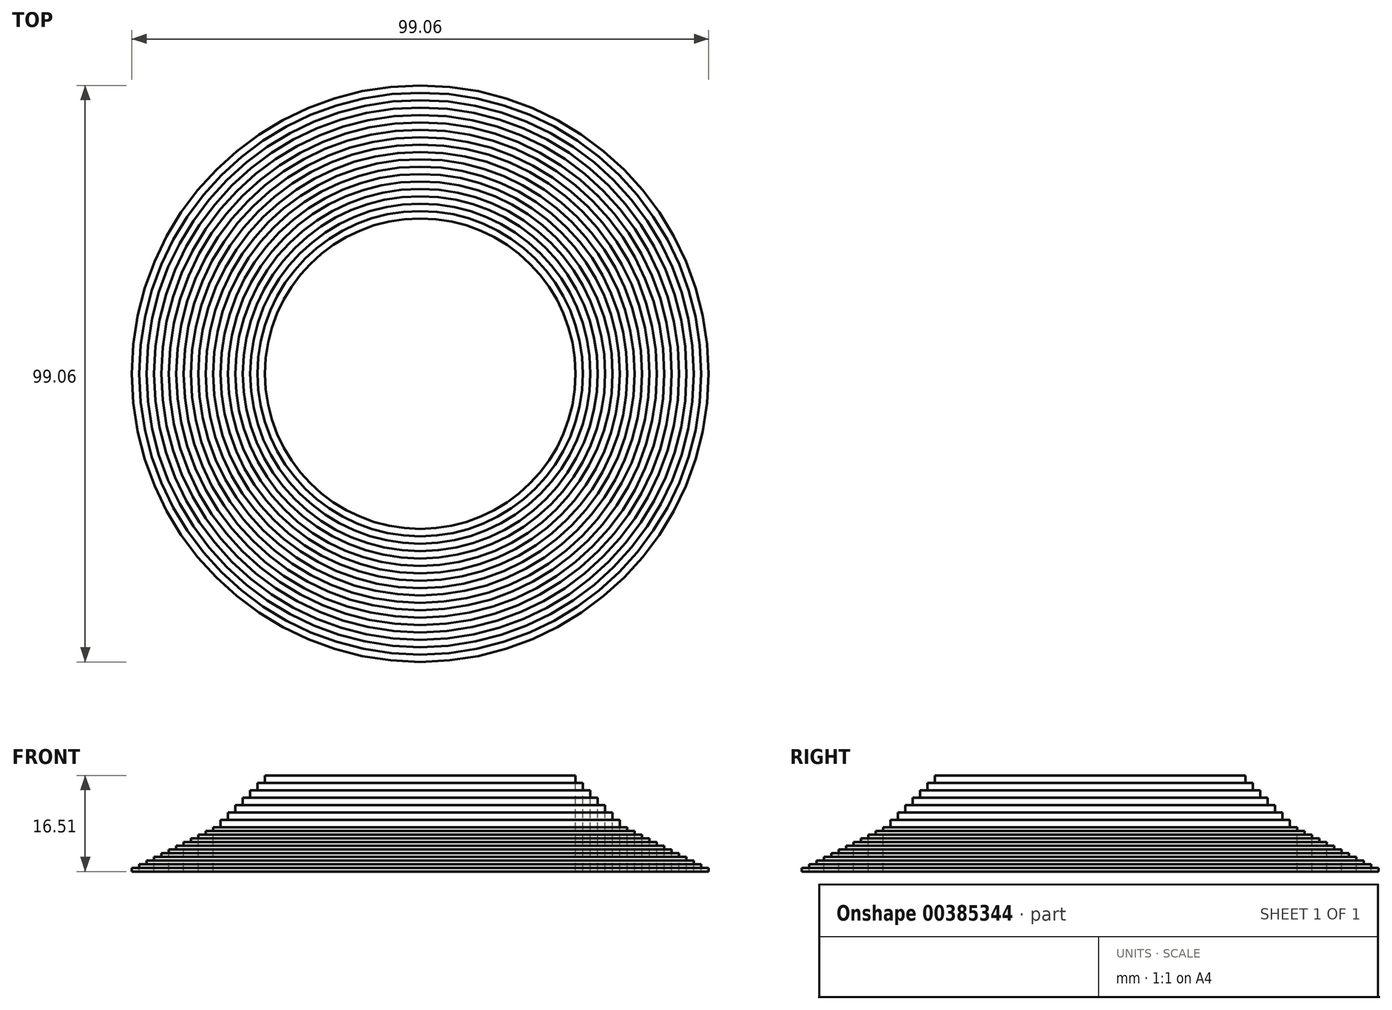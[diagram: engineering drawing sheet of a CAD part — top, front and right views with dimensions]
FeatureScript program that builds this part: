
annotation { "Feature Type Name" : "Feature", "Feature Type Description" : "" }
export const myFeature = defineFeature(function(context is Context, id is Id, definition is map)
    precondition{}
    {
        {
            var Q0;
            Q0=qCreatedBy(makeId("Top.planeOp"),FACE);
            var sketch = newSketch(context, id + "F0", { "sketchPlane" : qUnion([Q0])});
            skCircle(sketch, "E0", {"center": v(0, 0) * mm, "radius": 50.8 * mm});
            skSolve(sketch);
        }
        {
            var Q0;
            Q0=makeQuery(id+"F0.imprint","IMPRINT",FACE,{"disambiguationData":[TD([[makeQuery(id+"F0.imprint","IMPRINT",EDGE,{"derivedFrom":sQuery(id+"F0.wireOp",EDGE,"E0")}),1.0]])]});
            var sketch = newSketch(context, id + "F1", { "sketchPlane" : qUnion([Q0])});
            skCircle(sketch, "E1", {"center": v(0, 0) * mm, "radius": 49.53 * mm});
            skSolve(sketch);
        }
        {
            var Q0;
            Q0=sQuery(id+"F1.wireOp",EDGE,"E1");
            extrude(context, id + "F2", {"bodyType" : ToolBodyType.SURFACE, "surfaceEntities" : qUnion([Q0]), "depth" : 0.64 * mm});
        }
        {
            var Q0;
            Q0=makeQuery(id+"F0.imprint","IMPRINT",FACE,{"disambiguationData":[TD([[makeQuery(id+"F0.imprint","IMPRINT",EDGE,{"derivedFrom":sQuery(id+"F0.wireOp",EDGE,"E0")}),1.0]])]});
            var sketch = newSketch(context, id + "F3", { "sketchPlane" : qUnion([Q0])});
            skCircle(sketch, "E2", {"center": v(0, 0) * mm, "radius": 48.26 * mm});
            skSolve(sketch);
        }
        {
            var Q0;
            Q0=sQuery(id+"F3.wireOp",EDGE,"E2");
            extrude(context, id + "F4", {"bodyType" : ToolBodyType.SURFACE, "surfaceEntities" : qUnion([Q0]), "depth" : 1.27 * mm});
        }
        {
            var Q0;
            Q0=makeQuery(id+"F0.imprint","IMPRINT",FACE,{"disambiguationData":[TD([[makeQuery(id+"F0.imprint","IMPRINT",EDGE,{"derivedFrom":sQuery(id+"F0.wireOp",EDGE,"E0")}),1.0]])]});
            var sketch = newSketch(context, id + "F5", { "sketchPlane" : qUnion([Q0])});
            skCircle(sketch, "E3", {"center": v(0, 0) * mm, "radius": 47 * mm});
            skSolve(sketch);
        }
        {
            var Q0;
            Q0=sQuery(id+"F5.wireOp",EDGE,"E3");
            extrude(context, id + "F6", {"bodyType" : ToolBodyType.SURFACE, "surfaceEntities" : qUnion([Q0]), "depth" : 1.9 * mm});
        }
        {
            var Q0;
            Q0=makeQuery(id+"F0.imprint","IMPRINT",FACE,{"disambiguationData":[TD([[makeQuery(id+"F0.imprint","IMPRINT",EDGE,{"derivedFrom":sQuery(id+"F0.wireOp",EDGE,"E0")}),1.0]])]});
            var sketch = newSketch(context, id + "F7", { "sketchPlane" : qUnion([Q0])});
            skCircle(sketch, "E4", {"center": v(0, 0) * mm, "radius": 45.72 * mm});
            skSolve(sketch);
        }
        {
            var Q0;
            Q0=sQuery(id+"F7.wireOp",EDGE,"E4");
            extrude(context, id + "F8", {"bodyType" : ToolBodyType.SURFACE, "surfaceEntities" : qUnion([Q0]), "depth" : 2.54 * mm});
        }
        {
            var Q0;
            Q0=makeQuery(id+"F0.imprint","IMPRINT",FACE,{"disambiguationData":[TD([[makeQuery(id+"F0.imprint","IMPRINT",EDGE,{"derivedFrom":sQuery(id+"F0.wireOp",EDGE,"E0")}),1.0]])]});
            var sketch = newSketch(context, id + "F9", { "sketchPlane" : qUnion([Q0])});
            skCircle(sketch, "E5", {"center": v(0, 0) * mm, "radius": 44.45 * mm});
            skSolve(sketch);
        }
        {
            var Q0;
            Q0=sQuery(id+"F9.wireOp",EDGE,"E5");
            extrude(context, id + "F10", {"bodyType" : ToolBodyType.SURFACE, "surfaceEntities" : qUnion([Q0]), "depth" : 3.17 * mm});
        }
        {
            var Q0;
            Q0=makeQuery(id+"F0.imprint","IMPRINT",FACE,{"disambiguationData":[TD([[makeQuery(id+"F0.imprint","IMPRINT",EDGE,{"derivedFrom":sQuery(id+"F0.wireOp",EDGE,"E0")}),1.0]])]});
            var sketch = newSketch(context, id + "F11", { "sketchPlane" : qUnion([Q0])});
            skCircle(sketch, "E6", {"center": v(0, 0) * mm, "radius": 43.18 * mm});
            skSolve(sketch);
        }
        {
            var Q0;
            Q0=sQuery(id+"F11.wireOp",EDGE,"E6");
            extrude(context, id + "F12", {"bodyType" : ToolBodyType.SURFACE, "surfaceEntities" : qUnion([Q0]), "depth" : 3.8 * mm});
        }
        {
            var Q0;
            Q0=makeQuery(id+"F0.imprint","IMPRINT",FACE,{"disambiguationData":[TD([[makeQuery(id+"F0.imprint","IMPRINT",EDGE,{"derivedFrom":sQuery(id+"F0.wireOp",EDGE,"E0")}),1.0]])]});
            var sketch = newSketch(context, id + "F13", { "sketchPlane" : qUnion([Q0])});
            skCircle(sketch, "E7", {"center": v(0, 0) * mm, "radius": 41.91 * mm});
            skSolve(sketch);
        }
        {
            var Q0;
            Q0=sQuery(id+"F13.wireOp",EDGE,"E7");
            extrude(context, id + "F14", {"bodyType" : ToolBodyType.SURFACE, "surfaceEntities" : qUnion([Q0]), "depth" : 4.44 * mm});
        }
        {
            var Q0;
            Q0=makeQuery(id+"F0.imprint","IMPRINT",FACE,{"disambiguationData":[TD([[makeQuery(id+"F0.imprint","IMPRINT",EDGE,{"derivedFrom":sQuery(id+"F0.wireOp",EDGE,"E0")}),1.0]])]});
            var sketch = newSketch(context, id + "F15", { "sketchPlane" : qUnion([Q0])});
            skCircle(sketch, "E8", {"center": v(0, 0) * mm, "radius": 40.64 * mm});
            skSolve(sketch);
        }
        {
            var Q0;
            Q0=sQuery(id+"F15.wireOp",EDGE,"E8");
            extrude(context, id + "F16", {"bodyType" : ToolBodyType.SURFACE, "surfaceEntities" : qUnion([Q0]), "depth" : 5.08 * mm});
        }
        {
            var Q0;
            Q0=makeQuery(id+"F0.imprint","IMPRINT",FACE,{"disambiguationData":[TD([[makeQuery(id+"F0.imprint","IMPRINT",EDGE,{"derivedFrom":sQuery(id+"F0.wireOp",EDGE,"E0")}),1.0]])]});
            var sketch = newSketch(context, id + "F17", { "sketchPlane" : qUnion([Q0])});
            skCircle(sketch, "E9", {"center": v(0, 0) * mm, "radius": 39.37 * mm});
            skSolve(sketch);
        }
        {
            var Q0;
            Q0=sQuery(id+"F17.wireOp",EDGE,"E9");
            extrude(context, id + "F18", {"bodyType" : ToolBodyType.SURFACE, "surfaceEntities" : qUnion([Q0]), "depth" : 5.7 * mm});
        }
        {
            var Q0;
            Q0=makeQuery(id+"F0.imprint","IMPRINT",FACE,{"disambiguationData":[TD([[makeQuery(id+"F0.imprint","IMPRINT",EDGE,{"derivedFrom":sQuery(id+"F0.wireOp",EDGE,"E0")}),1.0]])]});
            var sketch = newSketch(context, id + "F19", { "sketchPlane" : qUnion([Q0])});
            skCircle(sketch, "E10", {"center": v(0, 0) * mm, "radius": 38.1 * mm});
            skSolve(sketch);
        }
        {
            var Q0;
            Q0=sQuery(id+"F19.wireOp",EDGE,"E10");
            extrude(context, id + "F20", {"bodyType" : ToolBodyType.SURFACE, "surfaceEntities" : qUnion([Q0]), "depth" : 6.35 * mm});
        }
        {
            var Q0;
            Q0=makeQuery(id+"F0.imprint","IMPRINT",FACE,{"disambiguationData":[TD([[makeQuery(id+"F0.imprint","IMPRINT",EDGE,{"derivedFrom":sQuery(id+"F0.wireOp",EDGE,"E0")}),1.0]])]});
            var sketch = newSketch(context, id + "F21", { "sketchPlane" : qUnion([Q0])});
            skCircle(sketch, "E11", {"center": v(0, 0) * mm, "radius": 36.83 * mm});
            skSolve(sketch);
        }
        {
            var Q0;
            Q0=sQuery(id+"F21.wireOp",EDGE,"E11");
            extrude(context, id + "F22", {"bodyType" : ToolBodyType.SURFACE, "surfaceEntities" : qUnion([Q0]), "depth" : 7 * mm});
        }
        {
            var Q0;
            Q0=makeQuery(id+"F0.imprint","IMPRINT",FACE,{"disambiguationData":[TD([[makeQuery(id+"F0.imprint","IMPRINT",EDGE,{"derivedFrom":sQuery(id+"F0.wireOp",EDGE,"E0")}),1.0]])]});
            var sketch = newSketch(context, id + "F23", { "sketchPlane" : qUnion([Q0])});
            skCircle(sketch, "E12", {"center": v(0, 0) * mm, "radius": 35.56 * mm});
            skSolve(sketch);
        }
        {
            var Q0;
            Q0=sQuery(id+"F23.wireOp",EDGE,"E12");
            extrude(context, id + "F24", {"bodyType" : ToolBodyType.SURFACE, "surfaceEntities" : qUnion([Q0]), "depth" : 7.62 * mm});
        }
        {
            var Q0;
            Q0=makeQuery(id+"F0.imprint","IMPRINT",FACE,{"disambiguationData":[TD([[makeQuery(id+"F0.imprint","IMPRINT",EDGE,{"derivedFrom":sQuery(id+"F0.wireOp",EDGE,"E0")}),1.0]])]});
            var sketch = newSketch(context, id + "F25", { "sketchPlane" : qUnion([Q0])});
            skCircle(sketch, "E13", {"center": v(0, 0) * mm, "radius": 34.3 * mm});
            skSolve(sketch);
        }
        {
            var Q0;
            Q0=sQuery(id+"F25.wireOp",EDGE,"E13");
            extrude(context, id + "F26", {"bodyType" : ToolBodyType.SURFACE, "surfaceEntities" : qUnion([Q0]), "depth" : 8.9 * mm});
        }
        {
            var Q0;
            Q0=makeQuery(id+"F0.imprint","IMPRINT",FACE,{"disambiguationData":[TD([[makeQuery(id+"F0.imprint","IMPRINT",EDGE,{"derivedFrom":sQuery(id+"F0.wireOp",EDGE,"E0")}),1.0]])]});
            var sketch = newSketch(context, id + "F27", { "sketchPlane" : qUnion([Q0])});
            skCircle(sketch, "E14", {"center": v(0, 0) * mm, "radius": 33.02 * mm});
            skSolve(sketch);
        }
        {
            var Q0;
            Q0=sQuery(id+"F27.wireOp",EDGE,"E14");
            extrude(context, id + "F28", {"bodyType" : ToolBodyType.SURFACE, "surfaceEntities" : qUnion([Q0]), "depth" : 10.16 * mm});
        }
        {
            var Q0;
            Q0=makeQuery(id+"F0.imprint","IMPRINT",FACE,{"disambiguationData":[TD([[makeQuery(id+"F0.imprint","IMPRINT",EDGE,{"derivedFrom":sQuery(id+"F0.wireOp",EDGE,"E0")}),1.0]])]});
            var sketch = newSketch(context, id + "F29", { "sketchPlane" : qUnion([Q0])});
            skCircle(sketch, "E15", {"center": v(0, 0) * mm, "radius": 31.75 * mm});
            skSolve(sketch);
        }
        {
            var Q0;
            Q0=sQuery(id+"F29.wireOp",EDGE,"E15");
            extrude(context, id + "F30", {"bodyType" : ToolBodyType.SURFACE, "surfaceEntities" : qUnion([Q0]), "depth" : 11.43 * mm});
        }
        {
            var Q0;
            Q0=makeQuery(id+"F0.imprint","IMPRINT",FACE,{"disambiguationData":[TD([[makeQuery(id+"F0.imprint","IMPRINT",EDGE,{"derivedFrom":sQuery(id+"F0.wireOp",EDGE,"E0")}),1.0]])]});
            var sketch = newSketch(context, id + "F31", { "sketchPlane" : qUnion([Q0])});
            skCircle(sketch, "E16", {"center": v(0, 0) * mm, "radius": 30.48 * mm});
            skSolve(sketch);
        }
        {
            var Q0;
            Q0=sQuery(id+"F31.wireOp",EDGE,"E16");
            extrude(context, id + "F32", {"bodyType" : ToolBodyType.SURFACE, "surfaceEntities" : qUnion([Q0]), "depth" : 12.7 * mm});
        }
        {
            var Q0;
            Q0=makeQuery(id+"F0.imprint","IMPRINT",FACE,{"disambiguationData":[TD([[makeQuery(id+"F0.imprint","IMPRINT",EDGE,{"derivedFrom":sQuery(id+"F0.wireOp",EDGE,"E0")}),1.0]])]});
            var sketch = newSketch(context, id + "F33", { "sketchPlane" : qUnion([Q0])});
            skCircle(sketch, "E17", {"center": v(0, 0) * mm, "radius": 29.21 * mm});
            skSolve(sketch);
        }
        {
            var Q0;
            Q0=sQuery(id+"F33.wireOp",EDGE,"E17");
            extrude(context, id + "F34", {"bodyType" : ToolBodyType.SURFACE, "surfaceEntities" : qUnion([Q0]), "depth" : 13.97 * mm});
        }
        {
            var Q0;
            Q0=makeQuery(id+"F0.imprint","IMPRINT",FACE,{"disambiguationData":[TD([[makeQuery(id+"F0.imprint","IMPRINT",EDGE,{"derivedFrom":sQuery(id+"F0.wireOp",EDGE,"E0")}),1.0]])]});
            var sketch = newSketch(context, id + "F35", { "sketchPlane" : qUnion([Q0])});
            skCircle(sketch, "E18", {"center": v(0, 0) * mm, "radius": 27.94 * mm});
            skSolve(sketch);
        }
        {
            var Q0;
            Q0=sQuery(id+"F35.wireOp",EDGE,"E18");
            extrude(context, id + "F36", {"bodyType" : ToolBodyType.SURFACE, "surfaceEntities" : qUnion([Q0]), "depth" : 15.24 * mm});
        }
        {
            var Q0;
            Q0=makeQuery(id+"F0.imprint","IMPRINT",FACE,{"disambiguationData":[TD([[makeQuery(id+"F0.imprint","IMPRINT",EDGE,{"derivedFrom":sQuery(id+"F0.wireOp",EDGE,"E0")}),1.0]])]});
            var sketch = newSketch(context, id + "F37", { "sketchPlane" : qUnion([Q0])});
            skCircle(sketch, "E19", {"center": v(0, 0) * mm, "radius": 26.67 * mm});
            skSolve(sketch);
        }
        {
            var Q0;
            Q0=sQuery(id+"F37.wireOp",EDGE,"E19");
            extrude(context, id + "F38", {"bodyType" : ToolBodyType.SURFACE, "surfaceEntities" : qUnion([Q0]), "depth" : 16.5 * mm});
        }
    });
